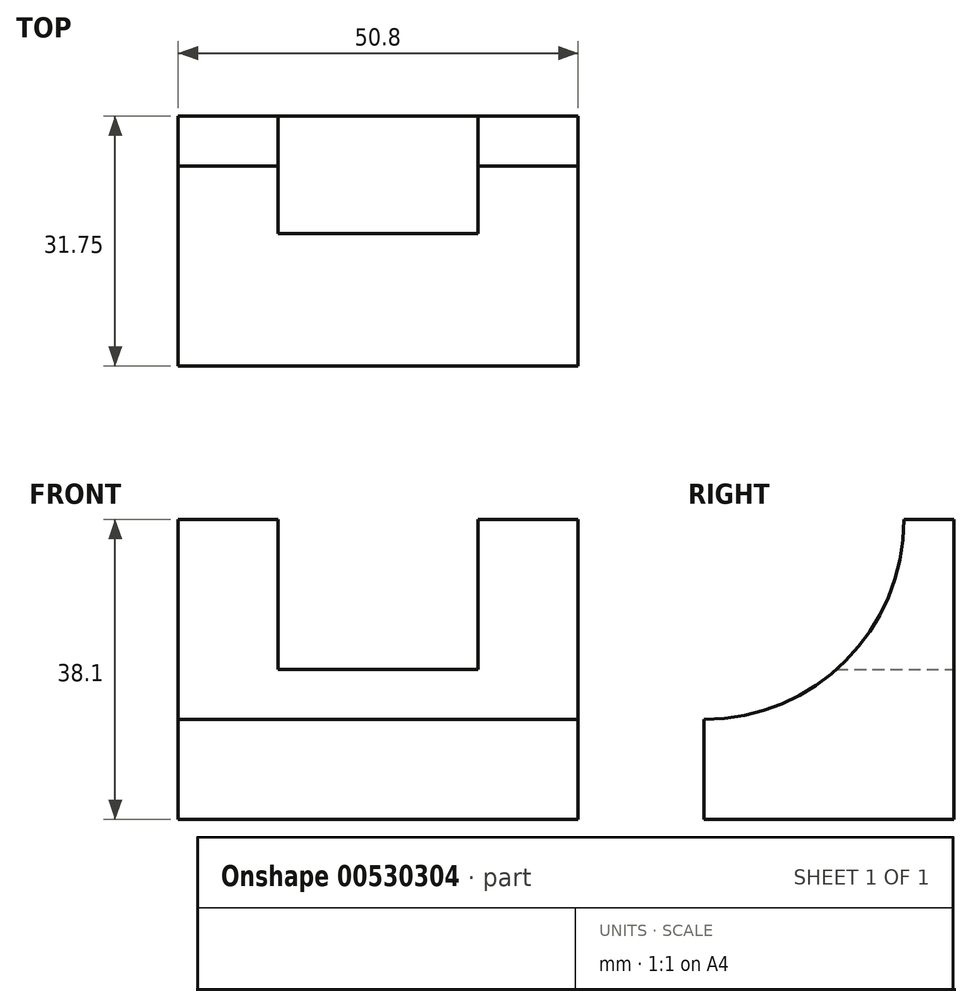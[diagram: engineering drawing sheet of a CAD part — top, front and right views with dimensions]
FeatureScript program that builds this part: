
annotation { "Feature Type Name" : "Feature", "Feature Type Description" : "" }
export const myFeature = defineFeature(function(context is Context, id is Id, definition is map)
    precondition{}
    {
        {
            var Q0;
            Q0=qCreatedBy(makeId("Front.planeOp"),FACE);
            var sketch = newSketch(context, id + "F0", { "sketchPlane" : qUnion([Q0])});
            skLineSegment(sketch, "E0", {"start": v(-38.57, 38.1) * mm, "end": v(-38.57, 0) * mm});
            skLineSegment(sketch, "E1", {"start": v(-38.57, 0) * mm, "end": v(12.23, 0) * mm});
            skLineSegment(sketch, "E2", {"start": v(12.23, 0) * mm, "end": v(12.23, 38.1) * mm});
            skLineSegment(sketch, "E3", {"start": v(12.23, 38.1) * mm, "end": v(-38.57, 38.1) * mm});
            skSolve(sketch);
        }
        {
            var Q0;
            Q0=makeQuery(id+"F0.imprint","IMPRINT",FACE,{"disambiguationData":[TD([[makeQuery(id+"F0.imprint","IMPRINT",EDGE,{"derivedFrom":sQuery(id+"F0.wireOp",EDGE,"E0")}),1.0]])]});
            extrude(context, id + "F1", {"entities" : qUnion([Q0]), "depth" : 31.75 * mm, "offsetDistance" : 25.4 * mm});
        }
        {
            var Q0;
            Q0=makeQuery(id+"F1.opExtrude","SWEPT_FACE",FACE,{"disambiguationData":[OSD([sQuery(id+"F0.wireOp",EDGE,"E2")])]});
            var sketch = newSketch(context, id + "F2", { "sketchPlane" : qUnion([Q0])});
            skLineSegment(sketch, "E4", {"start": v(0, 38.1) * mm, "end": v(-6.35, 38.1) * mm});
            skLineSegment(sketch, "E5", {"start": v(-31.75, 0) * mm, "end": v(-31.75, 12.7) * mm});
            skLineSegment(sketch, "E6", {"start": v(-31.75, 12.7) * mm, "end": v(0, 12.7) * mm});
            skLineSegment(sketch, "E7", {"start": v(-6.35, 38.1) * mm, "end": v(-6.35, 0) * mm});
            skArc(sketch, "E8", {"start": v(-31.75, 12.7) * mm, "mid": v(-13.79, 20.14) * mm, "end": v(-6.35, 38.1) * mm});
            skSolve(sketch);
        }
        {
            var Q0;
            {var subQ0=sQuery(id+"F2.wireOp",EDGE,"E8");Q0=makeQuery(id+"F2.imprint","IMPRINT",FACE,{"disambiguationData":[TD([[makeQuery(id+"F2.imprint","IMPRINT",EDGE,{"derivedFrom":subQ0}),1.0]])]});}
            extrude(context, id + "F3", {"entities" : qUnion([Q0]), "operationType" : NewBodyOperationType.REMOVE, "endBound" : BoundingType.THROUGH_ALL, "oppositeDirection" : true, "depth" : 25.4 * mm, "offsetDistance" : 25.4 * mm});
        }
        {
            var Q0;
            Q0=makeQuery(id+"F1.opExtrude","CAP_FACE",FACE,{"disambiguationData":[OSD([sQuery(id+"F0.wireOp",EDGE,"E0"),sQuery(id+"F0.wireOp",EDGE,"E1"),sQuery(id+"F0.wireOp",EDGE,"E2"),sQuery(id+"F0.wireOp",EDGE,"E3")])],"isStart":true});
            var sketch = newSketch(context, id + "F4", { "sketchPlane" : qUnion([Q0])});
            skPoint(sketch, "E9.endSnap0", {"position": v(38.57, 19.05) * mm});
            skLineSegment(sketch, "E10", {"start": v(38.57, 38.1) * mm, "end": v(25.87, 38.1) * mm});
            skLineSegment(sketch, "E11", {"start": v(25.87, 38.1) * mm, "end": v(25.87, 19.05) * mm});
            skLineSegment(sketch, "E12", {"start": v(25.87, 19.05) * mm, "end": v(0.47, 19.05) * mm});
            skLineSegment(sketch, "E13", {"start": v(0.47, 19.05) * mm, "end": v(0.47, 38.1) * mm});
            skLineSegment(sketch, "E14", {"start": v(0.47, 38.1) * mm, "end": v(-12.23, 38.1) * mm});
            skSolve(sketch);
        }
        {
            var Q0;
            {var subQ0=sQuery(id+"F4.wireOp",EDGE,"E11");Q0=makeQuery(id+"F4.imprint","IMPRINT",FACE,{"disambiguationData":[TD([[makeQuery(id+"F4.imprint","IMPRINT",EDGE,{"derivedFrom":subQ0}),-1.0]])]});}
            extrude(context, id + "F5", {"entities" : qUnion([Q0]), "operationType" : NewBodyOperationType.REMOVE, "endBound" : BoundingType.THROUGH_ALL, "oppositeDirection" : true, "depth" : 25.4 * mm, "offsetDistance" : 25.4 * mm});
        }
    });
